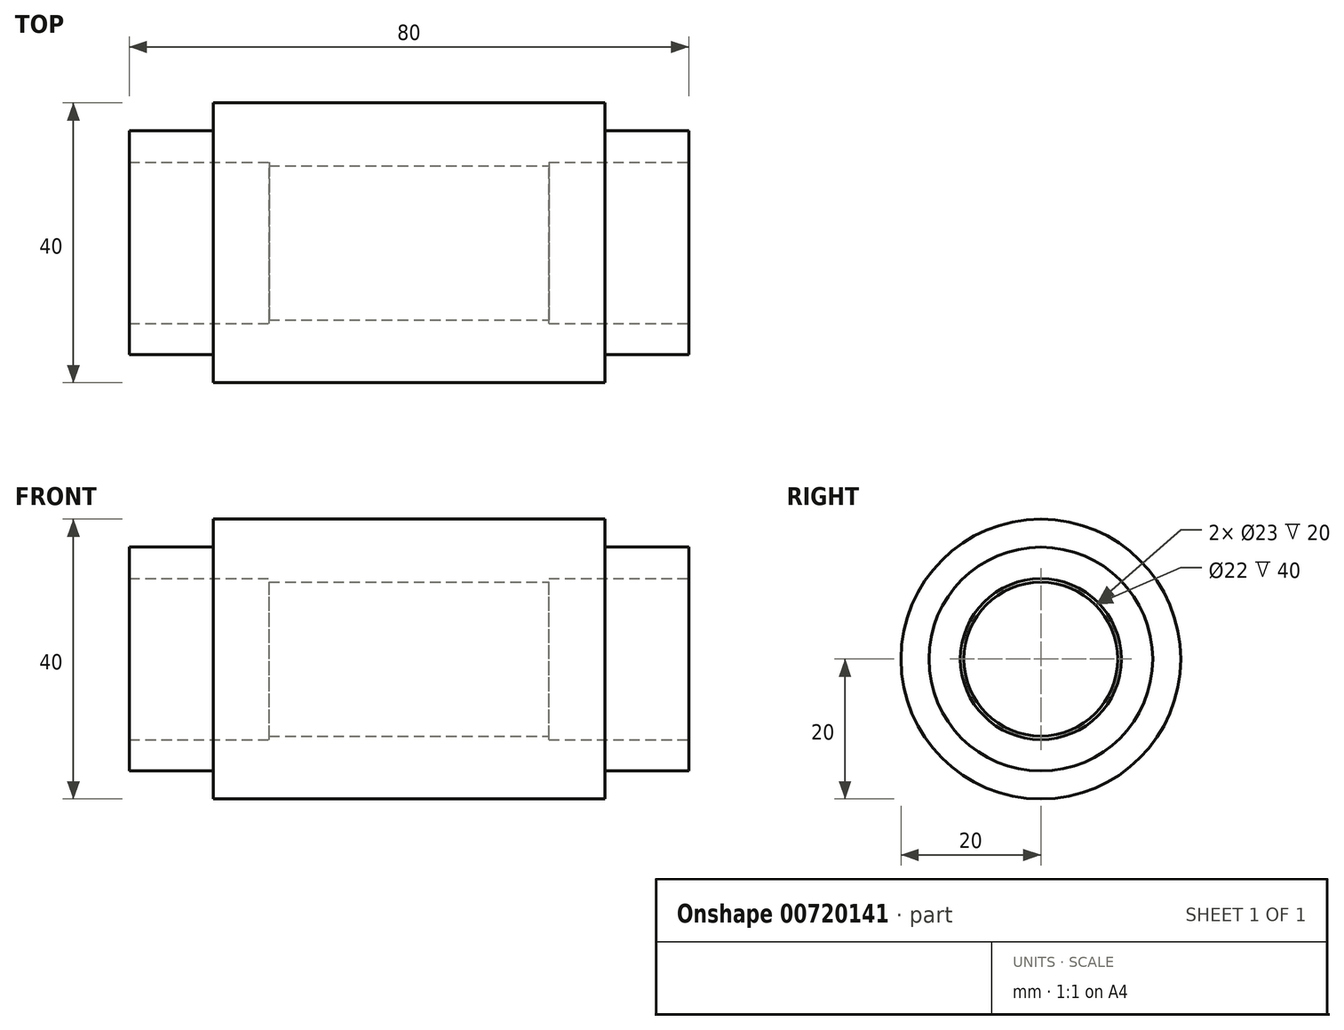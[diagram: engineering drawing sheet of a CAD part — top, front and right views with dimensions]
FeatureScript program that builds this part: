
annotation { "Feature Type Name" : "Feature", "Feature Type Description" : "" }
export const myFeature = defineFeature(function(context is Context, id is Id, definition is map)
    precondition{}
    {
        {
            var Q0;
            Q0=qCreatedBy(makeId("Front.planeOp"),FACE);
            var sketch = newSketch(context, id + "F0", { "sketchPlane" : qUnion([Q0])});
            skLineSegment(sketch, "E0", {"start": v(0, 0) * mm, "end": v(0, 16) * mm});
            skLineSegment(sketch, "E1", {"start": v(0, 16) * mm, "end": v(12, 16) * mm});
            skLineSegment(sketch, "E2", {"start": v(12, 16) * mm, "end": v(12, 20) * mm});
            skLineSegment(sketch, "E3", {"start": v(12, 20) * mm, "end": v(68, 20) * mm});
            skLineSegment(sketch, "E4", {"start": v(68, 20) * mm, "end": v(68, 16) * mm});
            skLineSegment(sketch, "E5", {"start": v(68, 16) * mm, "end": v(80, 16) * mm});
            skLineSegment(sketch, "E6", {"start": v(80, 16) * mm, "end": v(80, 0) * mm});
            skLineSegment(sketch, "E7", {"start": v(80, 0) * mm, "end": v(0, 0) * mm});
            skLineSegment(sketch, "E8.0", {"start": v(60, 11) * mm, "end": v(20, 11) * mm});
            skLineSegment(sketch, "E9.0", {"start": v(80, 11.5) * mm, "end": v(60, 11.5) * mm});
            skLineSegment(sketch, "E10.0", {"start": v(20, 11) * mm, "end": v(20, 11.5) * mm});
            skLineSegment(sketch, "E11.0", {"start": v(60, 11.5) * mm, "end": v(60, 11) * mm});
            skLineSegment(sketch, "E12.trimOffspring", {"start": v(20, 11.5) * mm, "end": v(0, 11.5) * mm});
            skSolve(sketch);
        }
        {
            var Q0;
            {var subQ3=sQuery(id+"F0.wireOp",EDGE,"E1");Q0=makeQuery(id+"F0.imprint","IMPRINT",FACE,{"disambiguationData":[TD([[makeQuery(id+"F0.imprint","IMPRINT",EDGE,{"derivedFrom":subQ3}),-1.0]])]});}
            var Q1;
            Q1=sQuery(id+"F0.wireOp",EDGE,"E7");
            revolve(context, id + "F1", {"surfaceOperationType" : NewSurfaceOperationType.NEW, "entities" : qUnion([Q0]), "axis" : qUnion([Q1]), "revolveType" : RevolveType.FULL});
        }
    });
